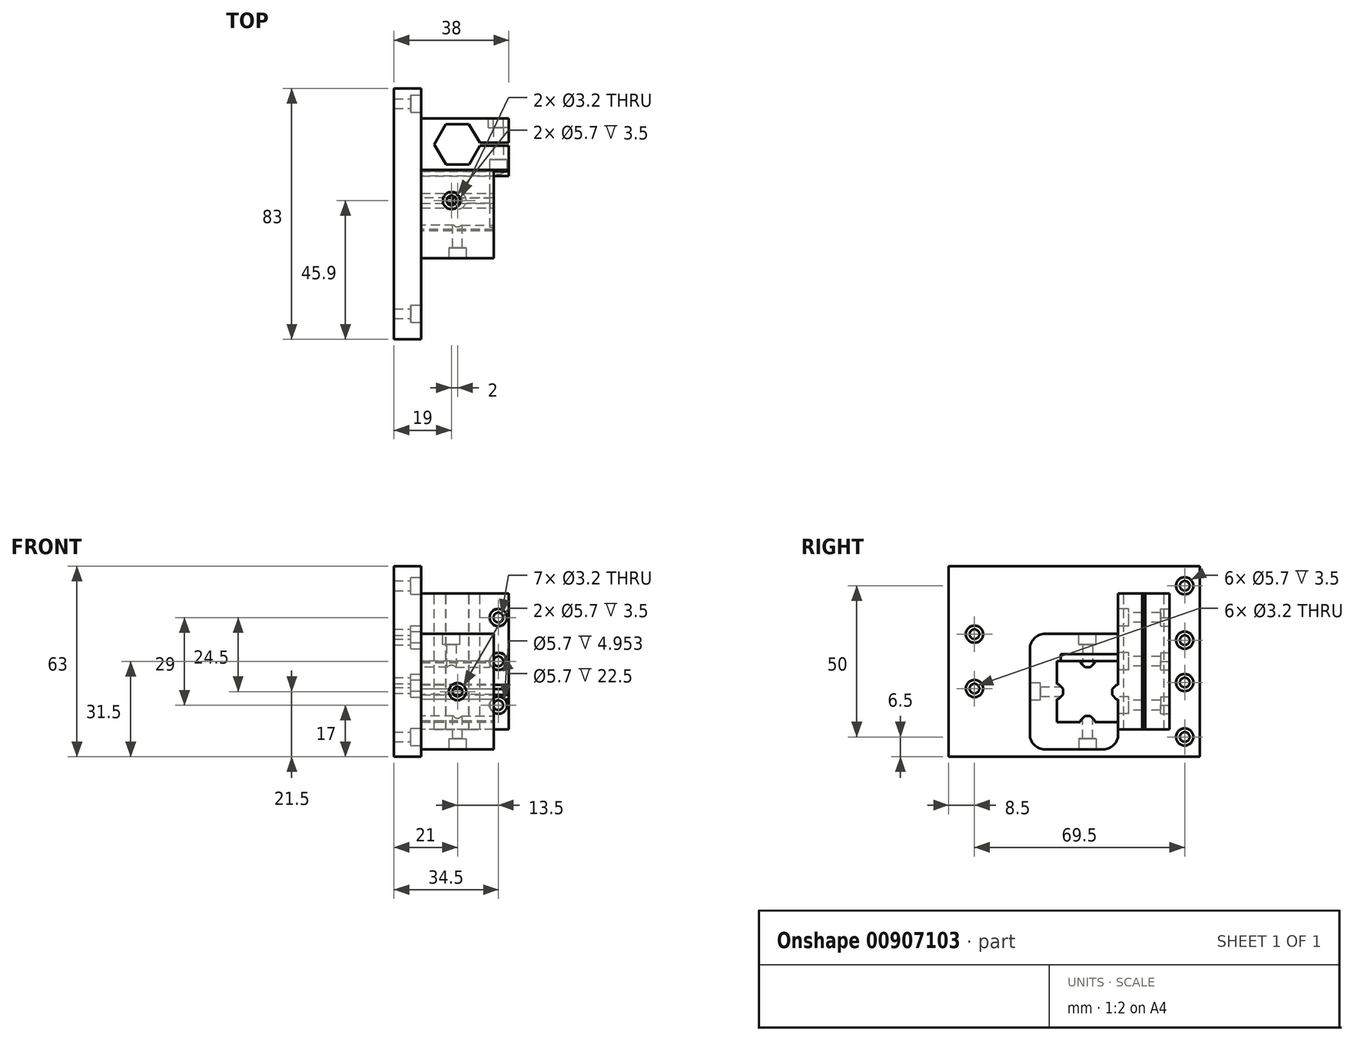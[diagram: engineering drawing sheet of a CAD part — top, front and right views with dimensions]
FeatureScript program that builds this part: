
annotation { "Feature Type Name" : "Feature", "Feature Type Description" : "" }
export const myFeature = defineFeature(function(context is Context, id is Id, definition is map)
    precondition{}
    {
        {
            assignVariable(context, id + "F0", {"name" : "headdepth", "anyValue" : 3.5 * mm});
        }
        {
            assignVariable(context, id + "F1", {"name" : "nutdepth", "anyValue" : 3});
        }
        {
            var Q0;
            Q0=qCreatedBy(makeId("Top.planeOp"),FACE);
            var sketch = newSketch(context, id + "F2", { "sketchPlane" : qUnion([Q0])});
            skLineSegment(sketch, "E0.bottom", {"start": v(0, 0) * mm, "end": v(9, 0) * mm});
            skLineSegment(sketch, "E0.top", {"start": v(0, 83) * mm, "end": v(9, 83) * mm});
            skLineSegment(sketch, "E0.left", {"start": v(0, 0) * mm, "end": v(0, 83) * mm});
            skLineSegment(sketch, "E0.right", {"start": v(9, 0) * mm, "end": v(9, 83) * mm});
            skSolve(sketch);
        }
        {
            var Q0;
            Q0=qSketchRegion(id+"F2",true);
            var Q1;
            Q1=makeQuery(id+"F2.imprint","IMPRINT",FACE,{"disambiguationData":[TD([[makeQuery(id+"F2.imprint","IMPRINT",EDGE,{"derivedFrom":sQuery(id+"F2.wireOp",EDGE,"E0.bottom")}),1.0]])]});
            extrude(context, id + "F3", {"entities" : qUnion([Q0, Q1]), "depth" : 63 * mm, "offsetDistance" : 25 * mm});
        }
        {
            var Q0;
            Q0=makeQuery(id+"F3.opExtrude","SWEPT_FACE",FACE,{"disambiguationData":[OSD([sQuery(id+"F2.wireOp",EDGE,"E0.right")])]});
            var sketch = newSketch(context, id + "F4", { "sketchPlane" : qUnion([Q0])});
            skLineSegment(sketch, "E1", {"start": v(83, 6.5) * mm, "end": v(0, 6.5) * mm, "construction": true});
            skLineSegment(sketch, "E2", {"start": v(0, 24.5) * mm, "end": v(83, 24.5) * mm, "construction": true});
            skLineSegment(sketch, "E3", {"start": v(83, 38.5) * mm, "end": v(0, 38.5) * mm, "construction": true});
            skLineSegment(sketch, "E4", {"start": v(0, 56.5) * mm, "end": v(83, 56.5) * mm, "construction": true});
            skLineSegment(sketch, "E5", {"start": v(78, 63) * mm, "end": v(78, 0) * mm, "construction": true});
            skLineSegment(sketch, "E6", {"start": v(8.5, 63) * mm, "end": v(8.5, 0) * mm, "construction": true});
            skLineSegment(sketch, "E7", {"start": v(0, 22.5) * mm, "end": v(8.5, 22.5) * mm, "construction": true});
            skLineSegment(sketch, "E8", {"start": v(0, 40.5) * mm, "end": v(8.5, 40.5) * mm, "construction": true});
            skCircle(sketch, "E9", {"center": v(8.5, 40.5) * mm, "radius": 2.85 * mm});
            skCircle(sketch, "E10", {"center": v(8.5, 22.5) * mm, "radius": 2.85 * mm});
            skCircle(sketch, "E11", {"center": v(78, 56.5) * mm, "radius": 2.85 * mm});
            skCircle(sketch, "E12", {"center": v(78, 38.5) * mm, "radius": 2.85 * mm});
            skCircle(sketch, "E13", {"center": v(78, 24.5) * mm, "radius": 2.85 * mm});
            skCircle(sketch, "E14", {"center": v(78, 6.5) * mm, "radius": 2.85 * mm});
            skSolve(sketch);
        }
        {
            var Q0;
            Q0=qSketchRegion(id+"F4",true);
            var Q1;
            Q1=makeQuery(id+"F4.imprint","IMPRINT",FACE,{"disambiguationData":[TD([[makeQuery(id+"F4.imprint","IMPRINT",EDGE,{"derivedFrom":sQuery(id+"F4.wireOp",EDGE,"E9")}),1.0]])]});
            extrude(context, id + "F5", {"entities" : qUnion([Q0, Q1]), "operationType" : NewBodyOperationType.REMOVE, "oppositeDirection" : true, "depth" : getVariable(context, 'headdepth'), "offsetDistance" : 25 * mm});
        }
        {
            var Q0;
            Q0=makeQuery(id+"F4.imprint","IMPRINT",FACE,{"disambiguationData":[TD([[makeQuery(id+"F4.imprint","IMPRINT",EDGE,{"derivedFrom":sQuery(id+"F4.wireOp",EDGE,"E9")}),1.0]])]});
            var sketch = newSketch(context, id + "F6", { "sketchPlane" : qUnion([Q0])});
            skCircle(sketch, "E15", {"center": v(8.5, 40.5) * mm, "radius": 1.6 * mm});
            skCircle(sketch, "E16", {"center": v(8.5, 22.5) * mm, "radius": 1.6 * mm});
            skCircle(sketch, "E17", {"center": v(78, 24.5) * mm, "radius": 1.6 * mm});
            skCircle(sketch, "E18", {"center": v(78, 38.5) * mm, "radius": 1.6 * mm});
            skCircle(sketch, "E19", {"center": v(78, 56.5) * mm, "radius": 1.6 * mm});
            skCircle(sketch, "E20", {"center": v(78, 6.5) * mm, "radius": 1.6 * mm});
            skSolve(sketch);
        }
        {
            var Q0;
            Q0=qSketchRegion(id+"F6",true);
            extrude(context, id + "F7", {"entities" : qUnion([Q0]), "operationType" : NewBodyOperationType.REMOVE, "oppositeDirection" : true, "depth" : 25 * mm, "offsetDistance" : 25 * mm});
        }
        {
            var Q0;
            Q0=makeQuery(id+"F4.imprint","IMPRINT",FACE,{"disambiguationData":[TD([[makeQuery(id+"F4.imprint","IMPRINT",EDGE,{"derivedFrom":sQuery(id+"F4.wireOp",EDGE,"E9")}),-1.0]])]});
            var sketch = newSketch(context, id + "F8", { "sketchPlane" : qUnion([Q0])});
            skLineSegment(sketch, "E21", {"start": v(64.5, 0) * mm, "end": v(64.5, 79.23) * mm, "construction": true});
            skLineSegment(sketch, "E22", {"start": v(0, 31.5) * mm, "end": v(82.89, 31.5) * mm, "construction": true});
            skLineSegment(sketch, "E23", {"start": v(0, 54) * mm, "end": v(83.05, 54) * mm, "construction": true});
            skLineSegment(sketch, "E24", {"start": v(0, 9) * mm, "end": v(83.14, 9) * mm, "construction": true});
            skLineSegment(sketch, "E25", {"start": v(56, 9) * mm, "end": v(56, 54) * mm});
            skLineSegment(sketch, "E26", {"start": v(73, 54) * mm, "end": v(73, 9) * mm});
            skLineSegment(sketch, "E27", {"start": v(56, 54) * mm, "end": v(73, 54) * mm});
            skLineSegment(sketch, "E28", {"start": v(73, 9) * mm, "end": v(56, 9) * mm});
            skLineSegment(sketch, "E29", {"start": v(56, 9) * mm, "end": v(56, 0) * mm, "construction": true});
            skLineSegment(sketch, "E30", {"start": v(56, 54) * mm, "end": v(56, 64.2) * mm, "construction": true});
            skSolve(sketch);
        }
        {
            var Q0;
            Q0=qSketchRegion(id+"F8",true);
            var Q1;
            Q1=makeQuery(id+"F8.imprint","IMPRINT",FACE,{"disambiguationData":[TD([[makeQuery(id+"F8.imprint","IMPRINT",EDGE,{"derivedFrom":sQuery(id+"F8.wireOp",EDGE,"E25")}),-1.0]])]});
            extrude(context, id + "F9", {"entities" : qUnion([Q0, Q1]), "operationType" : NewBodyOperationType.ADD, "depth" : 20 * mm, "offsetDistance" : 25 * mm});
        }
        {
            var Q0;
            Q0=makeQuery(id+"F9.opExtrude","SWEPT_FACE",FACE,{"disambiguationData":[OSD([sQuery(id+"F8.wireOp",EDGE,"E27")])]});
            var sketch = newSketch(context, id + "F10", { "sketchPlane" : qUnion([Q0])});
            skCircle(sketch, "E31.cCircle", {"center": v(21, 64.5) * mm, "radius": 6.65 * mm, "construction": true});
            skLineSegment(sketch, "E31.0", {"start": v(24.8, 71.17) * mm, "end": v(28.68, 64.55) * mm});
            skLineSegment(sketch, "E31.1", {"start": v(28.68, 64.55) * mm, "end": v(24.88, 57.87) * mm});
            skLineSegment(sketch, "E31.2", {"start": v(24.88, 57.87) * mm, "end": v(17.2, 57.83) * mm});
            skLineSegment(sketch, "E31.3", {"start": v(17.2, 57.83) * mm, "end": v(13.32, 64.45) * mm});
            skLineSegment(sketch, "E31.4", {"start": v(13.32, 64.45) * mm, "end": v(17.12, 71.13) * mm});
            skLineSegment(sketch, "E31.5", {"start": v(17.12, 71.13) * mm, "end": v(24.8, 71.17) * mm});
            skPoint(sketch, "E31.0.midPoint", {"position": v(26.74, 67.86) * mm});
            skLineSegment(sketch, "E32", {"start": v(21, 73) * mm, "end": v(21, 56) * mm, "construction": true});
            skLineSegment(sketch, "E33", {"start": v(29, 64.5) * mm, "end": v(9, 64.5) * mm, "construction": true});
            skSolve(sketch);
        }
        {
            var Q0;
            Q0=qSketchRegion(id+"F10",true);
            var Q1;
            Q1=makeQuery(id+"F10.imprint","IMPRINT",FACE,{"disambiguationData":[TD([[makeQuery(id+"F10.imprint","IMPRINT",EDGE,{"derivedFrom":sQuery(id+"F10.wireOp",EDGE,"E31.0")}),-1.0]])]});
            extrude(context, id + "F11", {"entities" : qUnion([Q0, Q1]), "operationType" : NewBodyOperationType.REMOVE, "oppositeDirection" : true, "depth" : 70 * mm, "offsetDistance" : 25 * mm});
        }
        {
            var Q0;
            Q0=makeQuery(id+"F9.opExtrude","CAP_FACE",FACE,{"disambiguationData":[OSD([sQuery(id+"F8.wireOp",EDGE,"E25"),sQuery(id+"F8.wireOp",EDGE,"E26"),sQuery(id+"F8.wireOp",EDGE,"E27"),sQuery(id+"F8.wireOp",EDGE,"E28")])],"isStart":false});
            var sketch = newSketch(context, id + "F12", { "sketchPlane" : qUnion([Q0])});
            skLineSegment(sketch, "E34", {"start": v(64.5, 54) * mm, "end": v(64.5, 9) * mm, "construction": true});
            skLineSegment(sketch, "E35", {"start": v(65, 54) * mm, "end": v(65, 9) * mm});
            skLineSegment(sketch, "E36", {"start": v(64, 54) * mm, "end": v(64, 9) * mm});
            skSolve(sketch);
        }
        {
            var Q0;
            Q0=qSketchRegion(id+"F12",true);
            var Q1;
            {var subQ0=sQuery(id+"F12.wireOp",EDGE,"E35");Q1=makeQuery(id+"F12.imprint","IMPRINT",FACE,{"disambiguationData":[TD([[makeQuery(id+"F12.imprint","IMPRINT",EDGE,{"derivedFrom":subQ0}),1.0]])]});}
            var Q2;
            {var subQ0=sQuery(id+"F12.wireOp",EDGE,"E36");Q2=makeQuery(id+"F12.imprint","IMPRINT",FACE,{"disambiguationData":[TD([[makeQuery(id+"F12.imprint","IMPRINT",EDGE,{"derivedFrom":subQ0}),-1.0]])]});}
            extrude(context, id + "F13", {"entities" : qUnion([Q0, Q1, Q2]), "operationType" : NewBodyOperationType.ADD, "depth" : 9 * mm, "offsetDistance" : 25 * mm});
        }
        {
            var Q0;
            Q0=qSketchRegion(id+"F12",true);
            var Q1;
            Q1=makeQuery(id+"F9.opExtrude","CAP_FACE",FACE,{"disambiguationData":[OSD([sQuery(id+"F8.wireOp",EDGE,"E25"),sQuery(id+"F8.wireOp",EDGE,"E26"),sQuery(id+"F8.wireOp",EDGE,"E27"),sQuery(id+"F8.wireOp",EDGE,"E28")])],"isStart":false});
            extrude(context, id + "F14", {"entities" : qUnion([Q0, Q1]), "operationType" : NewBodyOperationType.REMOVE, "oppositeDirection" : true, "depth" : 5 * mm, "offsetDistance" : 25 * mm});
        }
        {
            var Q0;
            {var subQ0=sQuery(id+"F8.wireOp",EDGE,"E25");Q0=makeQuery(id+"F13.boolean.opBoolean","MERGE",FACE,{"derivedFrom":[makeQuery(id+"F9.opExtrude","SWEPT_FACE",FACE,{"disambiguationData":[OSD([subQ0])]}),makeQuery(id+"F13.opExtrude","SWEPT_FACE",FACE,{"disambiguationData":[OSD([subQ0])]})]});}
            var sketch = newSketch(context, id + "F15", { "sketchPlane" : qUnion([Q0])});
            skLineSegment(sketch, "E37", {"start": v(34.5, 54) * mm, "end": v(34.5, 9) * mm, "construction": true});
            skLineSegment(sketch, "E38", {"start": v(34.5, 46) * mm, "end": v(38, 46) * mm, "construction": true});
            skLineSegment(sketch, "E39.1.0.0", {"start": v(34.5, 31.5) * mm, "end": v(38, 31.5) * mm, "construction": true});
            skLineSegment(sketch, "E39.2.0.0", {"start": v(34.5, 17) * mm, "end": v(38, 17) * mm, "construction": true});
            skLineSegment(sketch, "E39.direction1", {"start": v(34.5, 46) * mm, "end": v(34.5, 31.5) * mm, "construction": true});
            skCircle(sketch, "E40", {"center": v(34.5, 46) * mm, "radius": 2.85 * mm});
            skCircle(sketch, "E41", {"center": v(34.5, 31.5) * mm, "radius": 2.85 * mm});
            skCircle(sketch, "E42", {"center": v(34.5, 17) * mm, "radius": 2.85 * mm});
            skSolve(sketch);
        }
        {
            var Q0;
            Q0=qSketchRegion(id+"F15",true);
            extrude(context, id + "F16", {"entities" : qUnion([Q0]), "operationType" : NewBodyOperationType.REMOVE, "oppositeDirection" : true, "depth" : getVariable(context, 'headdepth'), "offsetDistance" : 25 * mm});
        }
        {
            var Q0;
            Q0=makeQuery(id+"F16.boolean.opBoolean","COPY",FACE,{"derivedFrom":makeQuery(id+"F16.opExtrude","CAP_FACE",FACE,{"disambiguationData":[OSD([sQuery(id+"F15.wireOp",EDGE,"E40")])],"isStart":false})});
            var sketch = newSketch(context, id + "F17", { "sketchPlane" : qUnion([Q0])});
            skCircle(sketch, "E43", {"center": v(34.5, 46) * mm, "radius": 1.6 * mm});
            skCircle(sketch, "E44", {"center": v(34.5, 31.5) * mm, "radius": 1.6 * mm});
            skCircle(sketch, "E45", {"center": v(34.5, 17) * mm, "radius": 1.6 * mm});
            skSolve(sketch);
        }
        {
            var Q0;
            Q0=qSketchRegion(id+"F17",true);
            extrude(context, id + "F18", {"entities" : qUnion([Q0]), "operationType" : NewBodyOperationType.REMOVE, "oppositeDirection" : true, "depth" : 25 * mm, "offsetDistance" : 25 * mm});
        }
        {
            var Q0;
            {var subQ0=sQuery(id+"F8.wireOp",EDGE,"E26");Q0=makeQuery(id+"F13.boolean.opBoolean","MERGE",FACE,{"derivedFrom":[makeQuery(id+"F9.opExtrude","SWEPT_FACE",FACE,{"disambiguationData":[OSD([subQ0])]}),makeQuery(id+"F13.opExtrude","SWEPT_FACE",FACE,{"disambiguationData":[OSD([subQ0])]})]});}
            var sketch = newSketch(context, id + "F19", { "sketchPlane" : qUnion([Q0])});
            skCircle(sketch, "E46.cCircle", {"center": v(-34.5, 46) * mm, "radius": 2.85 * mm, "construction": true});
            skLineSegment(sketch, "E46.0", {"start": v(-36.15, 48.85) * mm, "end": v(-32.85, 48.85) * mm});
            skLineSegment(sketch, "E46.1", {"start": v(-32.85, 48.85) * mm, "end": v(-31.2, 46) * mm});
            skLineSegment(sketch, "E46.2", {"start": v(-31.2, 46) * mm, "end": v(-32.85, 43.15) * mm});
            skLineSegment(sketch, "E46.3", {"start": v(-32.85, 43.15) * mm, "end": v(-36.15, 43.15) * mm});
            skLineSegment(sketch, "E46.4", {"start": v(-36.15, 43.15) * mm, "end": v(-37.8, 46) * mm});
            skLineSegment(sketch, "E46.5", {"start": v(-37.8, 46) * mm, "end": v(-36.15, 48.85) * mm});
            skPoint(sketch, "E46.0.midPoint", {"position": v(-34.5, 48.85) * mm});
            skCircle(sketch, "E47.cCircle", {"center": v(-34.5, 31.5) * mm, "radius": 2.85 * mm, "construction": true});
            skLineSegment(sketch, "E47.0", {"start": v(-36.15, 28.65) * mm, "end": v(-37.8, 31.5) * mm});
            skLineSegment(sketch, "E47.1", {"start": v(-37.8, 31.5) * mm, "end": v(-36.15, 34.35) * mm});
            skLineSegment(sketch, "E47.2", {"start": v(-36.15, 34.35) * mm, "end": v(-32.85, 34.35) * mm});
            skLineSegment(sketch, "E47.3", {"start": v(-32.85, 34.35) * mm, "end": v(-31.2, 31.5) * mm});
            skLineSegment(sketch, "E47.4", {"start": v(-31.2, 31.5) * mm, "end": v(-32.85, 28.65) * mm});
            skLineSegment(sketch, "E47.5", {"start": v(-32.85, 28.65) * mm, "end": v(-36.15, 28.65) * mm});
            skPoint(sketch, "E47.0.midPoint", {"position": v(-36.97, 30.07) * mm});
            skCircle(sketch, "E48.cCircle", {"center": v(-34.5, 17) * mm, "radius": 2.85 * mm, "construction": true});
            skLineSegment(sketch, "E48.0", {"start": v(-32.85, 19.85) * mm, "end": v(-31.2, 17) * mm});
            skLineSegment(sketch, "E48.1", {"start": v(-31.2, 17) * mm, "end": v(-32.85, 14.15) * mm});
            skLineSegment(sketch, "E48.2", {"start": v(-32.85, 14.15) * mm, "end": v(-36.15, 14.15) * mm});
            skLineSegment(sketch, "E48.3", {"start": v(-36.15, 14.15) * mm, "end": v(-37.8, 17) * mm});
            skLineSegment(sketch, "E48.4", {"start": v(-37.8, 17) * mm, "end": v(-36.15, 19.85) * mm});
            skLineSegment(sketch, "E48.5", {"start": v(-36.15, 19.85) * mm, "end": v(-32.85, 19.85) * mm});
            skPoint(sketch, "E48.0.midPoint", {"position": v(-32.03, 18.43) * mm});
            skSolve(sketch);
        }
        {
            var Q0;
            Q0=qSketchRegion(id+"F19",true);
            extrude(context, id + "F20", {"entities" : qUnion([Q0]), "operationType" : NewBodyOperationType.REMOVE, "oppositeDirection" : true, "depth" : (getVariable(context, 'nutdepth')) * mm, "offsetDistance" : 25 * mm});
        }
        {
            var Q0;
            Q0=makeQuery(id+"F4.imprint","IMPRINT",FACE,{"disambiguationData":[TD([[makeQuery(id+"F4.imprint","IMPRINT",EDGE,{"derivedFrom":sQuery(id+"F4.wireOp",EDGE,"E9")}),-1.0]])]});
            var sketch = newSketch(context, id + "F21", { "sketchPlane" : qUnion([Q0])});
            skLineSegment(sketch, "E49", {"start": v(0, 31.6) * mm, "end": v(83, 31.6) * mm, "construction": true});
            skLineSegment(sketch, "E50", {"start": v(0, 11.4) * mm, "end": v(83, 11.4) * mm, "construction": true});
            skLineSegment(sketch, "E51", {"start": v(35.8, 31.6) * mm, "end": v(35.8, 11.4) * mm, "construction": true});
            skLineSegment(sketch, "E52.bottom", {"start": v(35.8, 31.6) * mm, "end": v(26.8, 31.6) * mm});
            skLineSegment(sketch, "E52.top", {"start": v(35.8, 11.4) * mm, "end": v(26.8, 11.4) * mm});
            skLineSegment(sketch, "E52.left", {"start": v(35.8, 31.6) * mm, "end": v(35.8, 11.4) * mm});
            skLineSegment(sketch, "E52.right", {"start": v(26.8, 31.6) * mm, "end": v(26.8, 11.4) * mm});
            skLineSegment(sketch, "E53.bottom", {"start": v(56, 2.4) * mm, "end": v(26.8, 2.4) * mm});
            skLineSegment(sketch, "E53.top", {"start": v(56, 11.4) * mm, "end": v(26.8, 11.4) * mm});
            skLineSegment(sketch, "E53.left", {"start": v(56, 2.4) * mm, "end": v(56, 11.4) * mm});
            skLineSegment(sketch, "E53.right", {"start": v(26.8, 2.4) * mm, "end": v(26.8, 11.4) * mm});
            skLineSegment(sketch, "E54.bottom", {"start": v(56, 31.6) * mm, "end": v(26.8, 31.6) * mm});
            skLineSegment(sketch, "E54.top", {"start": v(56, 40.6) * mm, "end": v(26.8, 40.6) * mm});
            skLineSegment(sketch, "E54.left", {"start": v(56, 31.6) * mm, "end": v(56, 40.6) * mm});
            skLineSegment(sketch, "E54.right", {"start": v(26.8, 31.6) * mm, "end": v(26.8, 40.6) * mm});
            skSolve(sketch);
        }
        {
            var Q0;
            {var subQ0=makeQuery(id+"F21.imprint","IMPRINT",EDGE,{"derivedFrom":sQuery(id+"F21.wireOp",EDGE,"E52.top")});var subQ1=makeQuery(id+"F21.imprint","IMPRINT",EDGE,{"derivedFrom":sQuery(id+"F21.wireOp",EDGE,"E52.bottom")});Q0=qUnion([makeQuery(id+"F21.imprint","IMPRINT",FACE,{"disambiguationData":[TD([[subQ1,1.0]])]}),makeQuery(id+"F21.imprint","IMPRINT",FACE,{"disambiguationData":[TD([[subQ1,-1.0]])]}),makeQuery(id+"F21.imprint","IMPRINT",FACE,{"disambiguationData":[TD([[subQ0,1.0]])]})]);}
            var Q1;
            Q1=makeQuery(id+"F21.imprint","IMPRINT",FACE,{"disambiguationData":[TD([[makeQuery(id+"F21.imprint","IMPRINT",EDGE,{"derivedFrom":sQuery(id+"F21.wireOp",EDGE,"E52.bottom")}),1.0]])]});
            extrude(context, id + "F22", {"entities" : qUnion([Q0, Q1]), "operationType" : NewBodyOperationType.ADD, "depth" : 24 * mm, "offsetDistance" : 25 * mm});
        }
        {
            var Q0;
            Q0=makeQuery(id+"F22.opExtrude","SWEPT_FACE",FACE,{"disambiguationData":[OSD([sQuery(id+"F21.wireOp",EDGE,"E52.left")])]});
            var sketch = newSketch(context, id + "F23", { "sketchPlane" : qUnion([Q0])});
            skLineSegment(sketch, "E55", {"start": v(-9, 21.5) * mm, "end": v(-33, 21.5) * mm, "construction": true});
            skLineSegment(sketch, "E56.bottom", {"start": v(-9, 24) * mm, "end": v(-33, 24) * mm});
            skLineSegment(sketch, "E56.top", {"start": v(-9, 19) * mm, "end": v(-33, 19) * mm});
            skLineSegment(sketch, "E56.left", {"start": v(-9, 24) * mm, "end": v(-9, 19) * mm});
            skLineSegment(sketch, "E56.right", {"start": v(-33, 24) * mm, "end": v(-33, 19) * mm});
            skSolve(sketch);
        }
        {
            var Q0;
            Q0=qSketchRegion(id+"F23",true);
            extrude(context, id + "F24", {"entities" : qUnion([Q0]), "operationType" : NewBodyOperationType.ADD, "depth" : 2 * mm, "offsetDistance" : 25 * mm});
        }
        {
            var Q0;
            Q0=makeQuery(id+"F24.opExtrude","CAP_EDGE",EDGE,{"disambiguationData":[OSD([sQuery(id+"F23.wireOp",EDGE,"aU4TdgkL-9iKK-2Ztz-PjE2-94e6gGRGM6kK.top")])],"isStart":false});
            var Q1;
            Q1=makeQuery(id+"F24.opExtrude","CAP_EDGE",EDGE,{"disambiguationData":[OSD([sQuery(id+"F23.wireOp",EDGE,"aU4TdgkL-9iKK-2Ztz-PjE2-94e6gGRGM6kK.bottom")])],"isStart":false});
            var Q2;
            Q2=makeQuery(id+"F24.opExtrude","CAP_EDGE",EDGE,{"disambiguationData":[OSD([sQuery(id+"F23.wireOp",EDGE,"E56.bottom")])],"isStart":false});
            var Q3;
            Q3=makeQuery(id+"F24.opExtrude","CAP_EDGE",EDGE,{"disambiguationData":[OSD([sQuery(id+"F23.wireOp",EDGE,"E56.top")])],"isStart":false});
            chamfer(context, id + "F25", {"entities" : qUnion([Q0, Q1, Q2, Q3]), "width" : 1.5 * mm, "tangentPropagation" : true});
        }
        {
            var Q0;
            Q0=makeQuery(id+"F24.opExtrude","CAP_FACE",FACE,{"disambiguationData":[OSD([sQuery(id+"F23.wireOp",EDGE,"E56.bottom"),sQuery(id+"F23.wireOp",EDGE,"E56.top"),sQuery(id+"F23.wireOp",EDGE,"E56.left"),sQuery(id+"F23.wireOp",EDGE,"E56.right")])],"isStart":false});
            var sketch = newSketch(context, id + "F26", { "sketchPlane" : qUnion([Q0])});
            skLineSegment(sketch, "E57", {"start": v(-9, 21.5) * mm, "end": v(-33, 21.5) * mm, "construction": true});
            skLineSegment(sketch, "E58", {"start": v(-21, 20.5) * mm, "end": v(-21, 22.5) * mm, "construction": true});
            skCircle(sketch, "E59", {"center": v(-21, 21.5) * mm, "radius": 1.6 * mm});
            skSolve(sketch);
        }
        {
            var Q0;
            Q0=qSketchRegion(id+"F26",true);
            extrude(context, id + "F27", {"entities" : qUnion([Q0]), "operationType" : NewBodyOperationType.REMOVE, "oppositeDirection" : true, "depth" : 25 * mm, "offsetDistance" : 25 * mm});
        }
        {
            var Q0;
            Q0=makeQuery(id+"F15.imprint","IMPRINT",FACE,{"disambiguationData":[TD([[makeQuery(id+"F15.imprint","IMPRINT",EDGE,{"derivedFrom":sQuery(id+"F15.wireOp",EDGE,"E40")}),-1.0]])]});
            var sketch = newSketch(context, id + "F28", { "sketchPlane" : qUnion([Q0])});
            skLineSegment(sketch, "E60", {"start": v(38, 21.4) * mm, "end": v(9, 21.4) * mm, "construction": true});
            skLineSegment(sketch, "E61.bottom", {"start": v(9, 23.8) * mm, "end": v(38, 23.8) * mm});
            skLineSegment(sketch, "E61.top", {"start": v(9, 18.9) * mm, "end": v(38, 18.9) * mm});
            skLineSegment(sketch, "E61.left", {"start": v(9, 23.8) * mm, "end": v(9, 18.9) * mm});
            skLineSegment(sketch, "E61.right", {"start": v(38, 23.8) * mm, "end": v(38, 18.9) * mm});
            skSolve(sketch);
        }
        {
            var Q0;
            Q0=qSketchRegion(id+"F28",true);
            extrude(context, id + "F29", {"entities" : qUnion([Q0]), "operationType" : NewBodyOperationType.ADD, "depth" : 2 * mm, "offsetDistance" : 25 * mm});
        }
        {
            var Q0;
            Q0=makeQuery(id+"F29.opExtrude","CAP_EDGE",EDGE,{"disambiguationData":[OSD([sQuery(id+"F28.wireOp",EDGE,"E61.bottom")])],"isStart":false});
            var Q1;
            Q1=makeQuery(id+"F29.opExtrude","CAP_EDGE",EDGE,{"disambiguationData":[OSD([sQuery(id+"F28.wireOp",EDGE,"E61.top")])],"isStart":false});
            chamfer(context, id + "F30", {"entities" : qUnion([Q0, Q1]), "width" : 1.5 * mm, "tangentPropagation" : true});
        }
        {
            var Q0;
            Q0=qSketchRegion(id+"F15",true);
            extrude(context, id + "F31", {"entities" : qUnion([Q0]), "operationType" : NewBodyOperationType.REMOVE, "depth" : 19 * mm, "offsetDistance" : 25 * mm});
        }
        {
            var Q0;
            Q0=makeQuery(id+"F22.opExtrude","SWEPT_FACE",FACE,{"disambiguationData":[OSD([sQuery(id+"F21.wireOp",EDGE,"E53.top")])]});
            var sketch = newSketch(context, id + "F32", { "sketchPlane" : qUnion([Q0])});
            skLineSegment(sketch, "E62", {"start": v(9, 45.9) * mm, "end": v(33, 45.9) * mm, "construction": true});
            skLineSegment(sketch, "E63.bottom", {"start": v(9, 48.3) * mm, "end": v(33, 48.3) * mm});
            skLineSegment(sketch, "E63.top", {"start": v(9, 43.5) * mm, "end": v(33, 43.5) * mm});
            skLineSegment(sketch, "E63.left", {"start": v(9, 48.3) * mm, "end": v(9, 43.5) * mm});
            skLineSegment(sketch, "E63.right", {"start": v(33, 48.3) * mm, "end": v(33, 43.5) * mm});
            skSolve(sketch);
        }
        {
            var Q0;
            Q0=qSketchRegion(id+"F32",true);
            extrude(context, id + "F33", {"entities" : qUnion([Q0]), "operationType" : NewBodyOperationType.ADD, "depth" : 2 * mm, "offsetDistance" : 25 * mm});
        }
        {
            var Q0;
            Q0=makeQuery(id+"F33.opExtrude","CAP_EDGE",EDGE,{"disambiguationData":[OSD([sQuery(id+"F32.wireOp",EDGE,"E63.bottom")])],"isStart":false});
            var Q1;
            Q1=makeQuery(id+"F33.opExtrude","CAP_EDGE",EDGE,{"disambiguationData":[OSD([sQuery(id+"F32.wireOp",EDGE,"E63.top")])],"isStart":false});
            chamfer(context, id + "F34", {"entities" : qUnion([Q0, Q1]), "width" : 1.5 * mm, "tangentPropagation" : true});
        }
        {
            var Q0;
            Q0=makeQuery(id+"F33.opExtrude","CAP_FACE",FACE,{"disambiguationData":[OSD([sQuery(id+"F32.wireOp",EDGE,"E63.bottom"),sQuery(id+"F32.wireOp",EDGE,"E63.top"),sQuery(id+"F32.wireOp",EDGE,"E63.left"),sQuery(id+"F32.wireOp",EDGE,"E63.right")])],"isStart":false});
            var sketch = newSketch(context, id + "F35", { "sketchPlane" : qUnion([Q0])});
            skLineSegment(sketch, "E64", {"start": v(33, 45.9) * mm, "end": v(9, 45.9) * mm, "construction": true});
            skLineSegment(sketch, "E65", {"start": v(21, 46.8) * mm, "end": v(21, 45) * mm, "construction": true});
            skCircle(sketch, "E66", {"center": v(21, 45.9) * mm, "radius": 1.6 * mm});
            skSolve(sketch);
        }
        {
            var Q0;
            Q0=qSketchRegion(id+"F35",true);
            extrude(context, id + "F36", {"entities" : qUnion([Q0]), "operationType" : NewBodyOperationType.REMOVE, "oppositeDirection" : true, "depth" : 25 * mm, "offsetDistance" : 25 * mm});
        }
        {
            var Q0;
            Q0=makeQuery(id+"F22.opExtrude","SWEPT_FACE",FACE,{"disambiguationData":[OSD([sQuery(id+"F21.wireOp",EDGE,"E53.bottom")])]});
            var sketch = newSketch(context, id + "F37", { "sketchPlane" : qUnion([Q0])});
            skLineSegment(sketch, "E67", {"start": v(22.6, -45.9) * mm, "end": v(19.4, -45.9) * mm, "construction": true});
            skLineSegment(sketch, "E68", {"start": v(21, -47.5) * mm, "end": v(21, -44.3) * mm, "construction": true});
            skCircle(sketch, "E69", {"center": v(21, -45.9) * mm, "radius": 2.85 * mm});
            skSolve(sketch);
        }
        {
            var Q0;
            Q0=qSketchRegion(id+"F37",true);
            extrude(context, id + "F38", {"entities" : qUnion([Q0]), "operationType" : NewBodyOperationType.REMOVE, "oppositeDirection" : true, "depth" : getVariable(context, 'headdepth'), "offsetDistance" : 25 * mm});
        }
        {
            var Q0;
            Q0=makeQuery(id+"F22.opExtrude","SWEPT_FACE",FACE,{"disambiguationData":[OSD([sQuery(id+"F21.wireOp",EDGE,"E52.right"),sQuery(id+"F21.wireOp",EDGE,"E53.right"),sQuery(id+"F21.wireOp",EDGE,"E54.right")])]});
            var sketch = newSketch(context, id + "F39", { "sketchPlane" : qUnion([Q0])});
            skLineSegment(sketch, "E70", {"start": v(21, 23.1) * mm, "end": v(21, 19.9) * mm, "construction": true});
            skLineSegment(sketch, "E71", {"start": v(19.4, 21.5) * mm, "end": v(22.6, 21.5) * mm, "construction": true});
            skCircle(sketch, "E72", {"center": v(21, 21.5) * mm, "radius": 2.85 * mm});
            skSolve(sketch);
        }
        {
            var Q0;
            Q0=qSketchRegion(id+"F39",true);
            extrude(context, id + "F40", {"entities" : qUnion([Q0]), "operationType" : NewBodyOperationType.REMOVE, "oppositeDirection" : true, "depth" : getVariable(context, 'headdepth'), "offsetDistance" : 25 * mm});
        }
        {
            var Q0;
            Q0=makeQuery(id+"F22.opExtrude","SWEPT_EDGE",EDGE,{"disambiguationData":[OSD([sQuery(id+"F21.wireOp",EDGE,"E53.bottom"),sQuery(id+"F21.wireOp",EDGE,"E53.right")])]});
            var Q1;
            Q1=makeQuery(id+"F22.opExtrude","SWEPT_EDGE",EDGE,{"disambiguationData":[OSD([sQuery(id+"F21.wireOp",EDGE,"E54.top"),sQuery(id+"F21.wireOp",EDGE,"E54.right")])]});
            fillet(context, id + "F41", {"entities" : qUnion([Q0, Q1]), "radius" : 5 * mm, "tangentPropagation" : true, "allowEdgeOverflow" : false});
        }
        {
            var Q0;
            Q0=makeQuery(id+"F22.opExtrude","SWEPT_EDGE",EDGE,{"disambiguationData":[OSD([sQuery(id+"F21.wireOp",EDGE,"E53.bottom"),sQuery(id+"F21.wireOp",EDGE,"E53.left")])]});
            var Q1;
            Q1=makeQuery(id+"F22.opExtrude","SWEPT_EDGE",EDGE,{"disambiguationData":[OSD([sQuery(id+"F21.wireOp",EDGE,"E54.top"),sQuery(id+"F21.wireOp",EDGE,"E54.left")])]});
            fillet(context, id + "F42", {"entities" : qUnion([Q0, Q1]), "radius" : 5 * mm, "tangentPropagation" : true, "allowEdgeOverflow" : false});
        }
        {
            var Q0;
            Q0=makeQuery(id+"F22.opExtrude","SWEPT_FACE",FACE,{"disambiguationData":[OSD([sQuery(id+"F21.wireOp",EDGE,"E54.bottom")])]});
            var sketch = newSketch(context, id + "F43", { "sketchPlane" : qUnion([Q0])});
            skLineSegment(sketch, "E73", {"start": v(9, -45.9) * mm, "end": v(49.13, -45.9) * mm, "construction": true});
            skLineSegment(sketch, "E74.bottom", {"start": v(9, -43.5) * mm, "end": v(33, -43.5) * mm});
            skLineSegment(sketch, "E74.top", {"start": v(9, -48.3) * mm, "end": v(33, -48.3) * mm});
            skLineSegment(sketch, "E74.left", {"start": v(9, -43.5) * mm, "end": v(9, -48.3) * mm});
            skLineSegment(sketch, "E74.right", {"start": v(33, -43.5) * mm, "end": v(33, -48.3) * mm});
            skSolve(sketch);
        }
        {
            var Q0;
            {var subQ0=sQuery(id+"F43.wireOp",EDGE,"E74.left");Q0=makeQuery(id+"F43.imprint","IMPRINT",FACE,{"disambiguationData":[TD([[makeQuery(id+"F43.imprint","IMPRINT",EDGE,{"derivedFrom":subQ0}),-1.0]])]});}
            extrude(context, id + "F44", {"entities" : qUnion([Q0]), "operationType" : NewBodyOperationType.ADD, "depth" : 2 * mm, "offsetDistance" : 25 * mm});
        }
        {
            var Q0;
            Q0=makeQuery(id+"F44.opExtrude","CAP_EDGE",EDGE,{"disambiguationData":[OSD([sQuery(id+"F43.wireOp",EDGE,"E74.bottom")])],"isStart":false});
            var Q1;
            Q1=makeQuery(id+"F44.opExtrude","CAP_EDGE",EDGE,{"disambiguationData":[OSD([sQuery(id+"F43.wireOp",EDGE,"E74.top")])],"isStart":false});
            chamfer(context, id + "F45", {"entities" : qUnion([Q0, Q1]), "width" : 1.5 * mm, "tangentPropagation" : true});
        }
        {
            var Q0;
            Q0=makeQuery(id+"F44.opExtrude","CAP_FACE",FACE,{"disambiguationData":[OSD([sQuery(id+"F15.wireOp",EDGE,"E41"),sQuery(id+"F21.wireOp",EDGE,"E54.bottom"),sQuery(id+"F43.wireOp",EDGE,"E74.bottom"),sQuery(id+"F43.wireOp",EDGE,"E74.top"),sQuery(id+"F43.wireOp",EDGE,"E74.left")])],"isStart":false});
            var sketch = newSketch(context, id + "F46", { "sketchPlane" : qUnion([Q0])});
            skLineSegment(sketch, "E75", {"start": v(9, -45.9) * mm, "end": v(31.65, -45.9) * mm, "construction": true});
            skLineSegment(sketch, "E76", {"start": v(19, -45) * mm, "end": v(19, -46.8) * mm, "construction": true});
            skCircle(sketch, "E77", {"center": v(19, -45.9) * mm, "radius": 1.6 * mm});
            skSolve(sketch);
        }
        {
            var Q0;
            Q0 = qSketchRegion(id + "F46", true);
            extrude(context, id + "F47", {"entities" : qUnion([Q0]), "operationType" : NewBodyOperationType.REMOVE, "oppositeDirection" : true, "depth" : 25 * mm, "offsetDistance" : 25 * mm});
        }
        {
            var Q0;
            Q0=makeQuery(id+"F22.opExtrude","SWEPT_FACE",FACE,{"disambiguationData":[OSD([sQuery(id+"F21.wireOp",EDGE,"E54.top")])]});
            var sketch = newSketch(context, id + "F48", { "sketchPlane" : qUnion([Q0])});
            skLineSegment(sketch, "E78", {"start": v(19, 44.3) * mm, "end": v(19, 47.5) * mm, "construction": true});
            skLineSegment(sketch, "E79", {"start": v(17.4, 45.9) * mm, "end": v(20.6, 45.9) * mm, "construction": true});
            skCircle(sketch, "E80", {"center": v(19, 45.9) * mm, "radius": 2.85 * mm});
            skSolve(sketch);
        }
        {
            var Q0;
            Q0=makeQuery(id+"F48.imprint","IMPRINT",FACE,{"disambiguationData":[TD([[makeQuery(id+"F48.imprint","IMPRINT",EDGE,{"derivedFrom":makeQuery(id+"F47.boolean.opBoolean","INTERSECT",EDGE,{"derivedFrom":[makeQuery(id+"F22.opExtrude","SWEPT_FACE",FACE,{"disambiguationData":[OSD([sQuery(id+"F21.wireOp",EDGE,"E54.top")])]}),makeQuery(id+"F47.opExtrude","SWEPT_FACE",FACE,{"disambiguationData":[OSD([sQuery(id+"F46.wireOp",EDGE,"E77")])]})]})}),-1.0]])]});
            var Q1;
            Q1=makeQuery(id+"F48.imprint","IMPRINT",FACE,{"disambiguationData":[TD([[makeQuery(id+"F48.imprint","IMPRINT",EDGE,{"derivedFrom":sQuery(id+"F48.wireOp",EDGE,"E80")}),1.0]])]});
            extrude(context, id + "F49", {"entities" : qUnion([Q0, Q1]), "operationType" : NewBodyOperationType.REMOVE, "oppositeDirection" : true, "depth" : getVariable(context, 'headdepth'), "offsetDistance" : 25 * mm});
        }
    });
